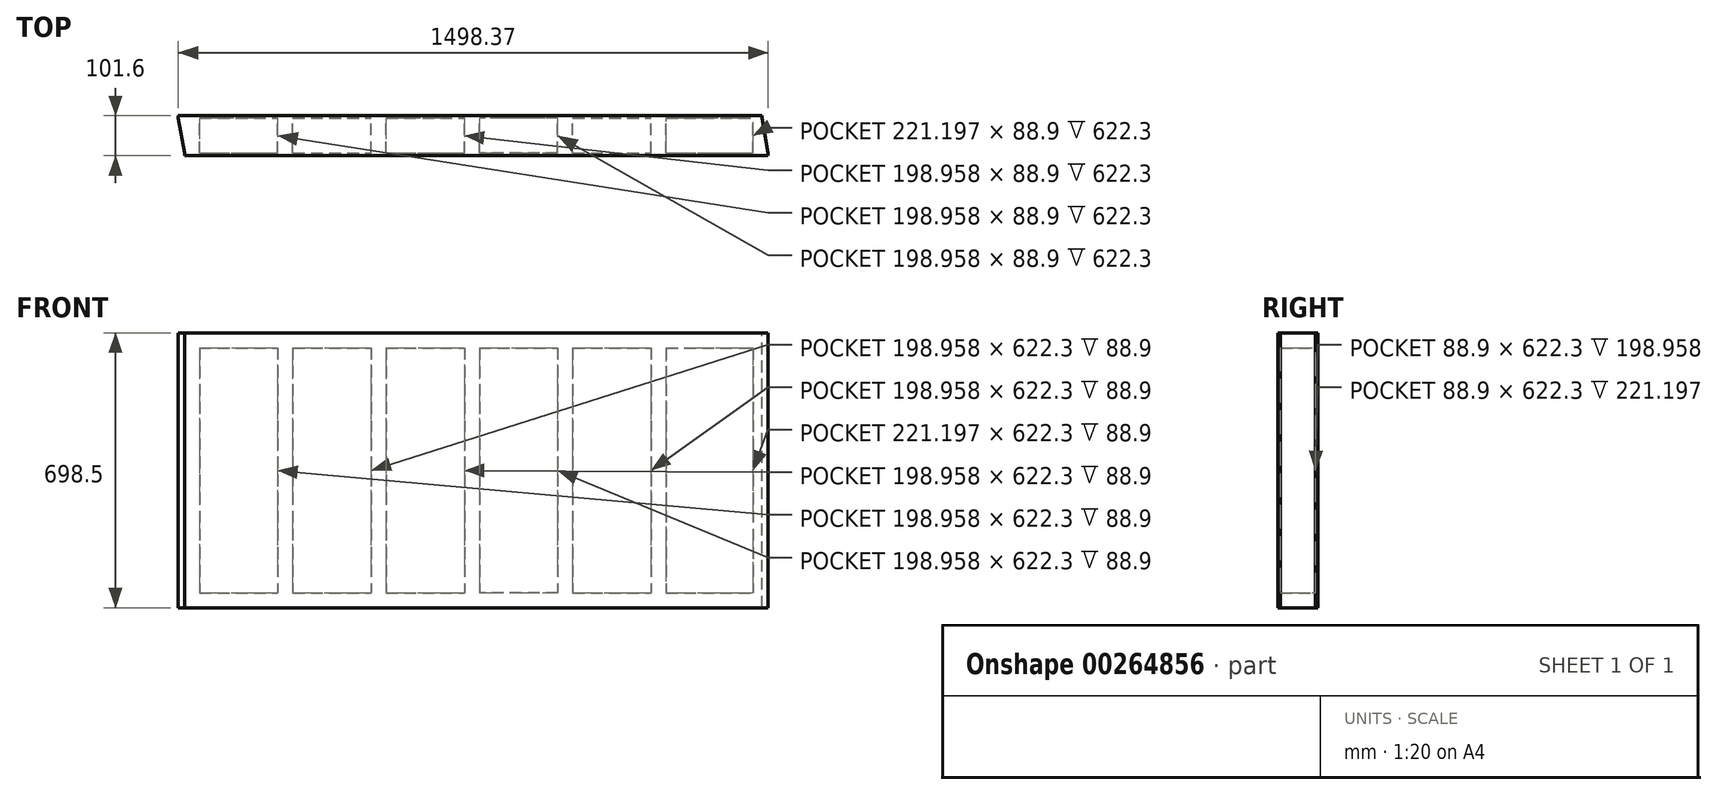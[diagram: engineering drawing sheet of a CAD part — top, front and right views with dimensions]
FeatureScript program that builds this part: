
annotation { "Feature Type Name" : "Feature", "Feature Type Description" : "" }
export const myFeature = defineFeature(function(context is Context, id is Id, definition is map)
    precondition{}
    {
        {
            var Q0;
            Q0=qCreatedBy(makeId("Front.planeOp"),FACE);
            var sketch = newSketch(context, id + "F0", { "sketchPlane" : qUnion([Q0])});
            skLineSegment(sketch, "E0.bottom", {"start": v(0, 0) * mm, "end": v(1482.69, 0) * mm});
            skLineSegment(sketch, "E0.top", {"start": v(0, 38.1) * mm, "end": v(237.06, 38.1) * mm});
            skLineSegment(sketch, "E0.left", {"start": v(0, 0) * mm, "end": v(0, 38.1) * mm});
            skLineSegment(sketch, "E0.right", {"start": v(1482.69, 0) * mm, "end": v(1482.69, 38.1) * mm});
            skLineSegment(sketch, "E1.bottom", {"start": v(38.1, 660.4) * mm, "end": v(237.06, 660.4) * mm});
            skLineSegment(sketch, "E1.top", {"start": v(0, 698.5) * mm, "end": v(1482.69, 698.5) * mm});
            skLineSegment(sketch, "E1.left", {"start": v(0, 660.4) * mm, "end": v(0, 698.5) * mm});
            skLineSegment(sketch, "E1.right", {"start": v(1482.69, 660.4) * mm, "end": v(1482.69, 698.5) * mm});
            skLineSegment(sketch, "E2.left", {"start": v(0, 660.4) * mm, "end": v(0, 38.1) * mm});
            skLineSegment(sketch, "E2.right", {"start": v(38.1, 660.4) * mm, "end": v(38.1, 38.1) * mm});
            skLineSegment(sketch, "E3.MirrorCS", {"start": v(1444.59, 660.4) * mm, "end": v(1444.59, 38.1) * mm});
            skLineSegment(sketch, "E4.MirrorCS", {"start": v(1482.69, 698.5) * mm, "end": v(1482.69, 38.1) * mm});
            skLineSegment(sketch, "E5", {"start": v(711.17, 660.4) * mm, "end": v(711.17, 38.1) * mm});
            skLineSegment(sketch, "E6.MirrorCS", {"start": v(749.27, 660.4) * mm, "end": v(749.27, 38.1) * mm});
            skLineSegment(sketch, "E7", {"start": v(474.12, 660.4) * mm, "end": v(474.12, 38.1) * mm});
            skLineSegment(sketch, "E8.MirrorCS", {"start": v(275.16, 660.4) * mm, "end": v(275.16, 38.1) * mm});
            skLineSegment(sketch, "E9.MirrorCS", {"start": v(237.06, 660.4) * mm, "end": v(237.06, 38.1) * mm});
            skLineSegment(sketch, "E10.MirrorCS", {"start": v(1223.4, 660.4) * mm, "end": v(1223.4, 38.1) * mm});
            skLineSegment(sketch, "E11.MirrorCS", {"start": v(1185.3, 660.4) * mm, "end": v(1185.3, 38.1) * mm});
            skLineSegment(sketch, "E12.trimOffspring", {"start": v(1223.4, 660.4) * mm, "end": v(1444.59, 660.4) * mm});
            skLineSegment(sketch, "E13.trimOffspring", {"start": v(986.33, 660.4) * mm, "end": v(1185.3, 660.4) * mm});
            skLineSegment(sketch, "E14.trimOffspring", {"start": v(986.33, 660.4) * mm, "end": v(986.33, 38.1) * mm});
            skLineSegment(sketch, "E15.trimOffspring", {"start": v(948.23, 660.4) * mm, "end": v(948.23, 38.1) * mm});
            skLineSegment(sketch, "E16.trimOffspring", {"start": v(749.27, 660.4) * mm, "end": v(948.23, 660.4) * mm});
            skLineSegment(sketch, "E17.trimOffspring", {"start": v(512.22, 660.4) * mm, "end": v(512.22, 38.1) * mm});
            skLineSegment(sketch, "E18.trimOffspring", {"start": v(512.22, 660.4) * mm, "end": v(711.17, 660.4) * mm});
            skLineSegment(sketch, "E19.trimOffspring", {"start": v(275.16, 660.4) * mm, "end": v(474.12, 660.4) * mm});
            skLineSegment(sketch, "E20.trimOffspring", {"start": v(275.16, 38.1) * mm, "end": v(474.12, 38.1) * mm});
            skLineSegment(sketch, "E21.trimOffspring", {"start": v(512.22, 38.1) * mm, "end": v(749.27, 38.1) * mm});
            skLineSegment(sketch, "E22.trimOffspring", {"start": v(986.33, 38.1) * mm, "end": v(1185.3, 38.1) * mm});
            skLineSegment(sketch, "E23", {"start": v(948.23, 38.1) * mm, "end": v(749.27, 38.1) * mm});
            skLineSegment(sketch, "E24.trimOffspring", {"start": v(1223.4, 38.1) * mm, "end": v(1444.59, 38.1) * mm});
            skSolve(sketch);
        }
        {
            var Q0;
            Q0=makeQuery(id+"F0.imprint","IMPRINT",FACE,{"disambiguationData":[TD([[makeQuery(id+"F0.imprint","IMPRINT",EDGE,{"derivedFrom":sQuery(id+"F0.wireOp",EDGE,"E1.top")}),-1.0]])]});
            var Q1;
            Q1=makeQuery(id+"F0.imprint","IMPRINT",FACE,{"disambiguationData":[TD([[makeQuery(id+"F0.imprint","IMPRINT",EDGE,{"derivedFrom":sQuery(id+"F0.wireOp",EDGE,"E0.bottom")}),1.0]])]});
            var Q2;
            Q2=makeQuery(id+"F0.imprint","IMPRINT",FACE,{"disambiguationData":[TD([[makeQuery(id+"F0.imprint","IMPRINT",EDGE,{"derivedFrom":sQuery(id+"F0.wireOp",EDGE,"E2.bottom")}),-1.0]])]});
            var Q3;
            {var subQ0=sQuery(id+"F0.wireOp",EDGE,"E8.MirrorCS");Q3=makeQuery(id+"F0.imprint","IMPRINT",FACE,{"disambiguationData":[TD([[makeQuery(id+"F0.imprint","IMPRINT",EDGE,{"derivedFrom":subQ0}),-1.0]])]});}
            var Q4;
            {var subQ0=sQuery(id+"F0.wireOp",EDGE,"E7");Q4=makeQuery(id+"F0.imprint","IMPRINT",FACE,{"disambiguationData":[TD([[makeQuery(id+"F0.imprint","IMPRINT",EDGE,{"derivedFrom":subQ0}),1.0]])]});}
            var Q5;
            {var subQ0=sQuery(id+"F0.wireOp",EDGE,"E5");Q5=makeQuery(id+"F0.imprint","IMPRINT",FACE,{"disambiguationData":[TD([[makeQuery(id+"F0.imprint","IMPRINT",EDGE,{"derivedFrom":subQ0}),1.0]])]});}
            var Q6;
            {var subQ0=sQuery(id+"F0.wireOp",EDGE,"f0f19201-27fc-4766-9588-adc457da11d90.MirrorCS");Q6=makeQuery(id+"F0.imprint","IMPRINT",FACE,{"disambiguationData":[TD([[makeQuery(id+"F0.imprint","IMPRINT",EDGE,{"derivedFrom":subQ0}),-1.0]])]});}
            var Q7;
            {var subQ0=sQuery(id+"F0.wireOp",EDGE,"E10.MirrorCS");Q7=makeQuery(id+"F0.imprint","IMPRINT",FACE,{"disambiguationData":[TD([[makeQuery(id+"F0.imprint","IMPRINT",EDGE,{"derivedFrom":subQ0}),-1.0]])]});}
            var Q8;
            {var subQ2=sQuery(id+"F0.wireOp",EDGE,"E3.MirrorCS");Q8=makeQuery(id+"F0.imprint","IMPRINT",FACE,{"disambiguationData":[TD([[makeQuery(id+"F0.imprint","IMPRINT",EDGE,{"derivedFrom":subQ2}),1.0]])]});}
            extrude(context, id + "F1", {"entities" : qUnion([Q0, Q1, Q2, Q3, Q4, Q5, Q6, Q7, Q8]), "depth" : 88.9 * mm, "offsetDistance" : 25.4 * mm});
        }
        {
            var Q0;
            Q0=makeQuery(id+"F1.opExtrude","SWEPT_FACE",FACE,{"disambiguationData":[OSD([sQuery(id+"F0.wireOp",EDGE,"E1.top")])]});
            var sketch = newSketch(context, id + "F2", { "sketchPlane" : qUnion([Q0])});
            skLineSegment(sketch, "E25", {"start": v(0, -88.9) * mm, "end": v(-49.74, 193.21) * mm});
            skLineSegment(sketch, "E26", {"start": v(-49.74, 193.21) * mm, "end": v(0, 193.21) * mm});
            skLineSegment(sketch, "E27", {"start": v(0, 193.21) * mm, "end": v(0, -88.9) * mm});
            skLineSegment(sketch, "E28", {"start": v(0, 0) * mm, "end": v(-15.68, 0) * mm});
            skSolve(sketch);
        }
        {
            var Q0;
            {var subQ4=sQuery(id+"F2.wireOp",EDGE,"E28");Q0=makeQuery(id+"F2.imprint","IMPRINT",FACE,{"disambiguationData":[TD([[makeQuery(id+"F2.imprint","IMPRINT",EDGE,{"derivedFrom":subQ4}),1.0]])]});}
            var Q1;
            Q1=makeQuery(id+"F1.opExtrude","SWEPT_FACE",FACE,{"disambiguationData":[OSD([sQuery(id+"F0.wireOp",EDGE,"E0.bottom")])]});
            extrude(context, id + "F3", {"entities" : qUnion([Q0]), "operationType" : NewBodyOperationType.ADD, "endBound" : BoundingType.UP_TO_SURFACE, "oppositeDirection" : true, "depth" : 25.4 * mm, "endBoundEntityFace" : qUnion([Q1]), "offsetDistance" : 25.4 * mm});
        }
        {
            var Q0;
            Q0=makeQuery(id+"F1.opExtrude","SWEPT_FACE",FACE,{"disambiguationData":[OSD([sQuery(id+"F0.wireOp",EDGE,"E1.top")])]});
            var sketch = newSketch(context, id + "F4", { "sketchPlane" : qUnion([Q0])});
            skLineSegment(sketch, "E29", {"start": v(1482.69, -88.9) * mm, "end": v(1442.71, 137.8) * mm});
            skLineSegment(sketch, "E30", {"start": v(1442.71, 137.8) * mm, "end": v(1482.69, 137.8) * mm});
            skLineSegment(sketch, "E31", {"start": v(1482.69, 137.8) * mm, "end": v(1482.69, -88.9) * mm});
            skLineSegment(sketch, "E32", {"start": v(1482.69, 0) * mm, "end": v(1467.01, 0) * mm});
            skSolve(sketch);
        }
        {
            var Q0;
            {var subQ4=sQuery(id+"F4.wireOp",EDGE,"E32");Q0=makeQuery(id+"F4.imprint","IMPRINT",FACE,{"disambiguationData":[TD([[makeQuery(id+"F4.imprint","IMPRINT",EDGE,{"derivedFrom":subQ4}),-1.0]])]});}
            extrude(context, id + "F5", {"entities" : qUnion([Q0]), "operationType" : NewBodyOperationType.REMOVE, "endBound" : BoundingType.THROUGH_ALL, "oppositeDirection" : true, "depth" : 25.4 * mm, "offsetDistance" : 25.4 * mm});
        }
        {
            var Q0;
            Q0=makeQuery(id+"F1.opExtrude","CAP_FACE",FACE,{"disambiguationData":[OSD([sQuery(id+"F0.wireOp",EDGE,"E0.bottom"),sQuery(id+"F0.wireOp",EDGE,"E0.top"),sQuery(id+"F0.wireOp",EDGE,"E0.left"),sQuery(id+"F0.wireOp",EDGE,"E0.right"),sQuery(id+"F0.wireOp",EDGE,"E1.bottom"),sQuery(id+"F0.wireOp",EDGE,"E1.top"),sQuery(id+"F0.wireOp",EDGE,"E1.left"),sQuery(id+"F0.wireOp",EDGE,"E2.left"),sQuery(id+"F0.wireOp",EDGE,"E2.right"),sQuery(id+"F0.wireOp",EDGE,"E3.MirrorCS"),sQuery(id+"F0.wireOp",EDGE,"E4.MirrorCS"),sQuery(id+"F0.wireOp",EDGE,"E5"),sQuery(id+"F0.wireOp",EDGE,"E6.MirrorCS"),sQuery(id+"F0.wireOp",EDGE,"E7"),sQuery(id+"F0.wireOp",EDGE,"E8.MirrorCS"),sQuery(id+"F0.wireOp",EDGE,"E9.MirrorCS"),sQuery(id+"F0.wireOp",EDGE,"E10.MirrorCS"),sQuery(id+"F0.wireOp",EDGE,"E11.MirrorCS"),sQuery(id+"F0.wireOp",EDGE,"E12.trimOffspring"),sQuery(id+"F0.wireOp",EDGE,"E13.trimOffspring"),sQuery(id+"F0.wireOp",EDGE,"E14.trimOffspring"),sQuery(id+"F0.wireOp",EDGE,"E15.trimOffspring"),sQuery(id+"F0.wireOp",EDGE,"E16.trimOffspring"),sQuery(id+"F0.wireOp",EDGE,"E17.trimOffspring"),sQuery(id+"F0.wireOp",EDGE,"E18.trimOffspring"),sQuery(id+"F0.wireOp",EDGE,"E19.trimOffspring"),sQuery(id+"F0.wireOp",EDGE,"E20.trimOffspring"),sQuery(id+"F0.wireOp",EDGE,"E21.trimOffspring"),sQuery(id+"F0.wireOp",EDGE,"E22.trimOffspring"),sQuery(id+"F0.wireOp",EDGE,"E23"),sQuery(id+"F0.wireOp",EDGE,"E24.trimOffspring")])],"isStart":false});
            var sketch = newSketch(context, id + "F6", { "sketchPlane" : qUnion([Q0])});
            skLineSegment(sketch, "E33.bottom", {"start": v(0, 698.5) * mm, "end": v(1482.69, 698.5) * mm});
            skLineSegment(sketch, "E33.top", {"start": v(0, 0) * mm, "end": v(1482.69, 0) * mm});
            skLineSegment(sketch, "E33.left", {"start": v(0, 698.5) * mm, "end": v(0, 0) * mm});
            skLineSegment(sketch, "E33.right", {"start": v(1482.69, 698.5) * mm, "end": v(1482.69, 0) * mm});
            skSolve(sketch);
        }
        {
            var Q0;
            Q0 = qSketchRegion(id + "F6", true);
            extrude(context, id + "F7", {"entities" : qUnion([Q0]), "operationType" : NewBodyOperationType.ADD, "depth" : 6.35 * mm, "offsetDistance" : 25.4 * mm});
        }
        {
            var Q0;
            Q0=makeQuery(id+"F3.boolean.opBoolean","MERGE",FACE,{"derivedFrom":[makeQuery(id+"F1.opExtrude","CAP_FACE",FACE,{"disambiguationData":[OSD([sQuery(id+"F0.wireOp",EDGE,"E0.bottom"),sQuery(id+"F0.wireOp",EDGE,"E0.top"),sQuery(id+"F0.wireOp",EDGE,"E0.left"),sQuery(id+"F0.wireOp",EDGE,"E0.right"),sQuery(id+"F0.wireOp",EDGE,"E1.bottom"),sQuery(id+"F0.wireOp",EDGE,"E1.top"),sQuery(id+"F0.wireOp",EDGE,"E1.left"),sQuery(id+"F0.wireOp",EDGE,"E2.left"),sQuery(id+"F0.wireOp",EDGE,"E2.right"),sQuery(id+"F0.wireOp",EDGE,"E3.MirrorCS"),sQuery(id+"F0.wireOp",EDGE,"E4.MirrorCS"),sQuery(id+"F0.wireOp",EDGE,"E5"),sQuery(id+"F0.wireOp",EDGE,"E6.MirrorCS"),sQuery(id+"F0.wireOp",EDGE,"E7"),sQuery(id+"F0.wireOp",EDGE,"E8.MirrorCS"),sQuery(id+"F0.wireOp",EDGE,"E9.MirrorCS"),sQuery(id+"F0.wireOp",EDGE,"E10.MirrorCS"),sQuery(id+"F0.wireOp",EDGE,"E11.MirrorCS"),sQuery(id+"F0.wireOp",EDGE,"E12.trimOffspring"),sQuery(id+"F0.wireOp",EDGE,"E13.trimOffspring"),sQuery(id+"F0.wireOp",EDGE,"E14.trimOffspring"),sQuery(id+"F0.wireOp",EDGE,"E15.trimOffspring"),sQuery(id+"F0.wireOp",EDGE,"E16.trimOffspring"),sQuery(id+"F0.wireOp",EDGE,"E17.trimOffspring"),sQuery(id+"F0.wireOp",EDGE,"E18.trimOffspring"),sQuery(id+"F0.wireOp",EDGE,"E19.trimOffspring"),sQuery(id+"F0.wireOp",EDGE,"E20.trimOffspring"),sQuery(id+"F0.wireOp",EDGE,"E21.trimOffspring"),sQuery(id+"F0.wireOp",EDGE,"E22.trimOffspring"),sQuery(id+"F0.wireOp",EDGE,"E23"),sQuery(id+"F0.wireOp",EDGE,"E24.trimOffspring")])],"isStart":true}),makeQuery(id+"F3.opExtrude","SWEPT_FACE",FACE,{"disambiguationData":[OSD([sQuery(id+"F2.wireOp",EDGE,"E28")])]})]});
            var sketch = newSketch(context, id + "F8", { "sketchPlane" : qUnion([Q0])});
            skLineSegment(sketch, "E34.bottom", {"start": v(-1467.01, 698.5) * mm, "end": v(15.68, 698.5) * mm});
            skLineSegment(sketch, "E34.top", {"start": v(-1467.01, 0) * mm, "end": v(15.68, 0) * mm});
            skLineSegment(sketch, "E34.left", {"start": v(-1467.01, 698.5) * mm, "end": v(-1467.01, 0) * mm});
            skLineSegment(sketch, "E34.right", {"start": v(15.68, 698.5) * mm, "end": v(15.68, 0) * mm});
            skSolve(sketch);
        }
        {
            var Q0;
            Q0 = qSketchRegion(id + "F8", true);
            extrude(context, id + "F9", {"entities" : qUnion([Q0]), "operationType" : NewBodyOperationType.ADD, "depth" : 6.35 * mm, "offsetDistance" : 25.4 * mm});
        }
    });
